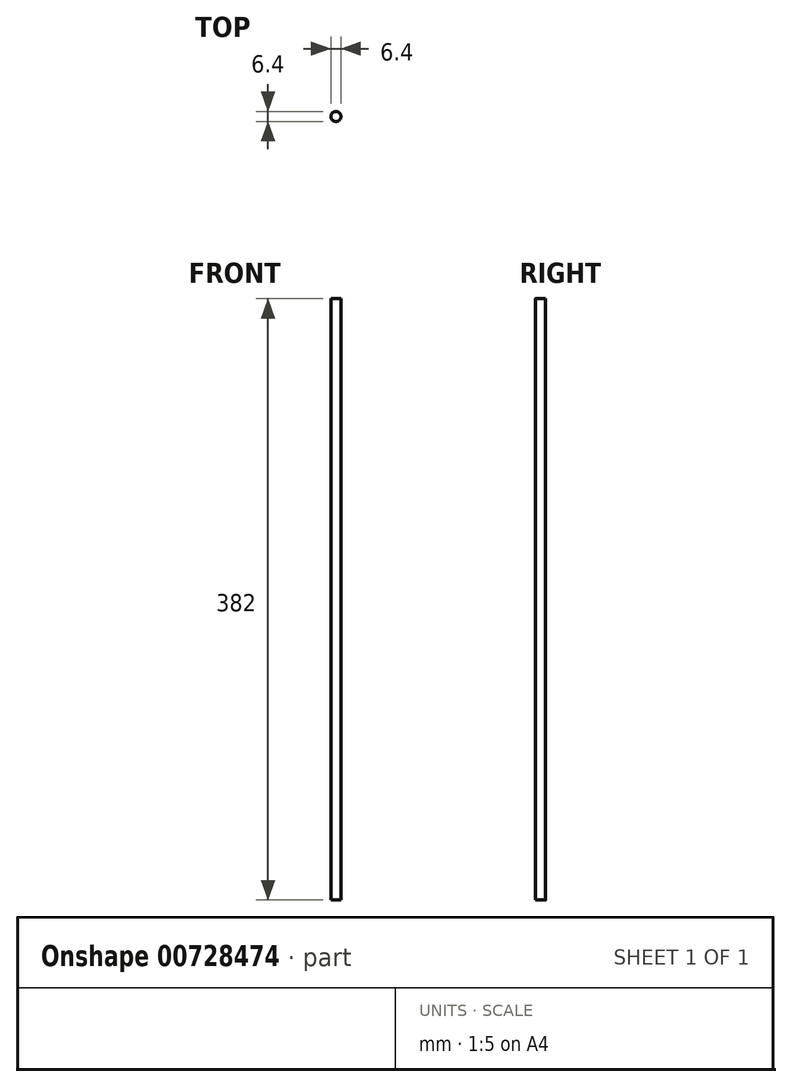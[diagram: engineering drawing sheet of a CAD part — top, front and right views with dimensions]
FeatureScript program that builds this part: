
annotation { "Feature Type Name" : "Feature", "Feature Type Description" : "" }
export const myFeature = defineFeature(function(context is Context, id is Id, definition is map)
    precondition{}
    {
        {
            var Q0;
            Q0=qCreatedBy(makeId("Top.planeOp"),FACE);
            cPlane(context, id + "F0", {"entities" : qUnion([Q0]), "cplaneType" : CPlaneType.OFFSET, "offset" : 27 * mm, "oppositeDirection" : true, "width" : 152.4 * mm, "height" : 152.4 * mm});
        }
        {
            var Q0;
            Q0=qCreatedBy(id+"F0.planeOp",FACE);
            var sketch = newSketch(context, id + "F1", { "sketchPlane" : qUnion([Q0])});
            skCircle(sketch, "E0", {"center": v(0, 0) * mm, "radius": 3.2 * mm});
            skSolve(sketch);
        }
        {
            var Q0;
            Q0=makeQuery(id+"F1.imprint","IMPRINT",FACE,{"disambiguationData":[TD([[makeQuery(id+"F1.imprint","IMPRINT",EDGE,{"derivedFrom":sQuery(id+"F1.wireOp",EDGE,"E0")}),1.0]])]});
            extrude(context, id + "F2", {"entities" : qUnion([Q0]), "oppositeDirection" : true, "depth" : 382 * mm, "offsetDistance" : 25 * mm});
        }
    });
